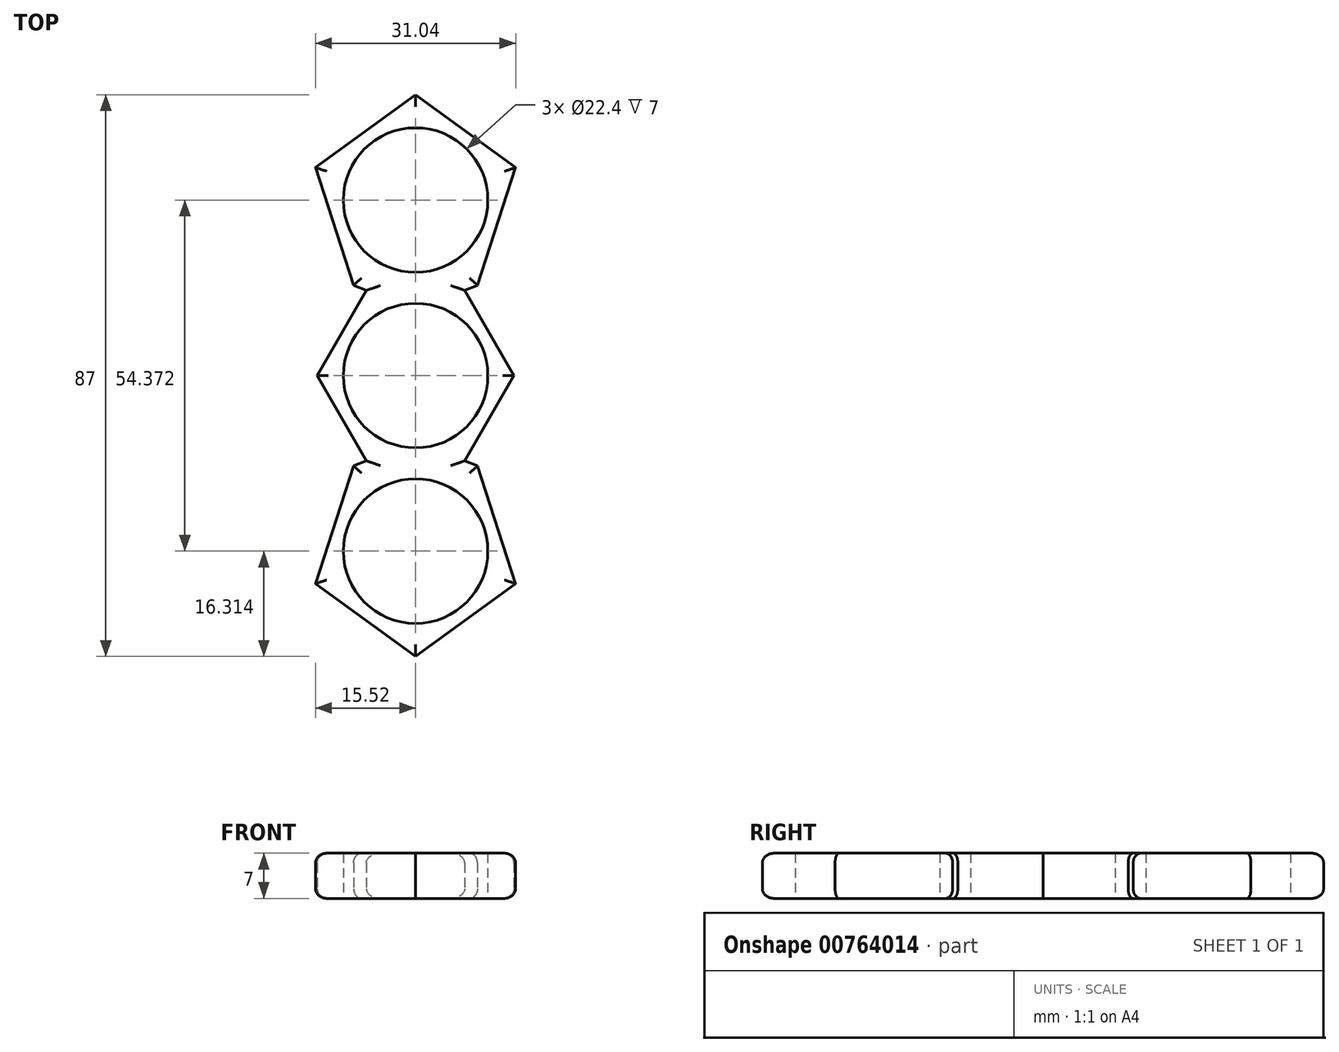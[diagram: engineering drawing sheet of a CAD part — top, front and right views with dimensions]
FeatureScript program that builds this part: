
annotation { "Feature Type Name" : "Feature", "Feature Type Description" : "" }
export const myFeature = defineFeature(function(context is Context, id is Id, definition is map)
    precondition{}
    {
        {
            var Q0;
            Q0=qCreatedBy(makeId("Top.planeOp"),FACE);
            var sketch = newSketch(context, id + "F0", { "sketchPlane" : qUnion([Q0])});
            skCircle(sketch, "E0", {"center": v(0, 0) * mm, "radius": 11.2 * mm});
            skCircle(sketch, "E1", {"center": v(0, 27.19) * mm, "radius": 11.2 * mm});
            skCircle(sketch, "E2.1.1", {"center": v(0, -27.19) * mm, "radius": 11.2 * mm});
            skLineSegment(sketch, "E3.1", {"start": v(-9.6, 13.99) * mm, "end": v(-15.52, 32.23) * mm});
            skLineSegment(sketch, "E3.2", {"start": v(-15.52, 32.23) * mm, "end": v(0, 43.5) * mm});
            skLineSegment(sketch, "E3.3", {"start": v(0, 43.5) * mm, "end": v(15.52, 32.23) * mm});
            skLineSegment(sketch, "E3.4", {"start": v(15.52, 32.23) * mm, "end": v(9.6, 13.99) * mm});
            skPoint(sketch, "E3.0.midPoint", {"position": v(0, 13.99) * mm});
            skLineSegment(sketch, "E4.1.1", {"start": v(-15.52, -32.23) * mm, "end": v(-9.6, -13.99) * mm});
            skLineSegment(sketch, "E4.1.2", {"start": v(0, -43.5) * mm, "end": v(-15.52, -32.23) * mm});
            skLineSegment(sketch, "E4.1.3", {"start": v(15.52, -32.23) * mm, "end": v(0, -43.5) * mm});
            skLineSegment(sketch, "E4.1.4", {"start": v(9.6, -13.99) * mm, "end": v(15.52, -32.23) * mm});
            skLineSegment(sketch, "E5.0", {"start": v(15.24, 0) * mm, "end": v(7.62, -13.2) * mm});
            skLineSegment(sketch, "E5.2", {"start": v(-7.62, -13.2) * mm, "end": v(-15.24, 0) * mm});
            skLineSegment(sketch, "E5.3", {"start": v(-15.24, 0) * mm, "end": v(-7.62, 13.2) * mm});
            skLineSegment(sketch, "E5.5", {"start": v(7.62, 13.2) * mm, "end": v(15.24, 0) * mm});
            skPoint(sketch, "E5.0.midPoint", {"position": v(11.43, -6.6) * mm});
            skLineSegment(sketch, "E6", {"start": v(-9.6, -13.99) * mm, "end": v(-7.62, -13.2) * mm});
            skLineSegment(sketch, "E7", {"start": v(9.6, -13.99) * mm, "end": v(7.62, -13.2) * mm});
            skLineSegment(sketch, "E8", {"start": v(7.62, 13.2) * mm, "end": v(9.6, 13.99) * mm});
            skLineSegment(sketch, "E9", {"start": v(-7.62, 13.2) * mm, "end": v(-9.6, 13.99) * mm});
            skSolve(sketch);
        }
        {
            var Q0;
            Q0=makeQuery(id+"F0.imprint","IMPRINT",FACE,{"disambiguationData":[TD([[makeQuery(id+"F0.imprint","IMPRINT",EDGE,{"derivedFrom":sQuery(id+"F0.wireOp",EDGE,"E0")}),-1.0]])]});
            extrude(context, id + "F1", {"entities" : qUnion([Q0]), "depth" : 7 * mm, "offsetDistance" : 25 * mm});
        }
        {
            var Q0;
            Q0=makeQuery(id+"F1.opExtrude","CAP_EDGE",EDGE,{"disambiguationData":[OSD([sQuery(id+"F0.wireOp",EDGE,"E4.1.1")])],"isStart":false});
            var Q1;
            Q1=makeQuery(id+"F1.opExtrude","CAP_EDGE",EDGE,{"disambiguationData":[OSD([sQuery(id+"F0.wireOp",EDGE,"E4.1.2")])],"isStart":false});
            var Q2;
            Q2=makeQuery(id+"F1.opExtrude","CAP_EDGE",EDGE,{"disambiguationData":[OSD([sQuery(id+"F0.wireOp",EDGE,"E4.1.3")])],"isStart":false});
            var Q3;
            Q3=makeQuery(id+"F1.opExtrude","CAP_EDGE",EDGE,{"disambiguationData":[OSD([sQuery(id+"F0.wireOp",EDGE,"E4.1.4")])],"isStart":false});
            var Q4;
            Q4=makeQuery(id+"F1.opExtrude","CAP_EDGE",EDGE,{"disambiguationData":[OSD([sQuery(id+"F0.wireOp",EDGE,"E6")])],"isStart":false});
            var Q5;
            Q5=makeQuery(id+"F1.opExtrude","CAP_EDGE",EDGE,{"disambiguationData":[OSD([sQuery(id+"F0.wireOp",EDGE,"E7")])],"isStart":false});
            var Q6;
            Q6=makeQuery(id+"F1.opExtrude","CAP_EDGE",EDGE,{"disambiguationData":[OSD([sQuery(id+"F0.wireOp",EDGE,"E8")])],"isStart":false});
            var Q7;
            Q7=makeQuery(id+"F1.opExtrude","CAP_EDGE",EDGE,{"disambiguationData":[OSD([sQuery(id+"F0.wireOp",EDGE,"E9")])],"isStart":false});
            var Q8;
            Q8=makeQuery(id+"F1.opExtrude","CAP_EDGE",EDGE,{"disambiguationData":[OSD([sQuery(id+"F0.wireOp",EDGE,"E5.3")])],"isStart":false});
            var Q9;
            Q9=makeQuery(id+"F1.opExtrude","CAP_EDGE",EDGE,{"disambiguationData":[OSD([sQuery(id+"F0.wireOp",EDGE,"E5.2")])],"isStart":false});
            var Q10;
            Q10=makeQuery(id+"F1.opExtrude","CAP_EDGE",EDGE,{"disambiguationData":[OSD([sQuery(id+"F0.wireOp",EDGE,"E5.0")])],"isStart":false});
            var Q11;
            Q11=makeQuery(id+"F1.opExtrude","CAP_EDGE",EDGE,{"disambiguationData":[OSD([sQuery(id+"F0.wireOp",EDGE,"E5.5")])],"isStart":false});
            var Q12;
            Q12=makeQuery(id+"F1.opExtrude","CAP_EDGE",EDGE,{"disambiguationData":[OSD([sQuery(id+"F0.wireOp",EDGE,"E3.4")])],"isStart":false});
            var Q13;
            Q13=makeQuery(id+"F1.opExtrude","CAP_EDGE",EDGE,{"disambiguationData":[OSD([sQuery(id+"F0.wireOp",EDGE,"E3.3")])],"isStart":false});
            var Q14;
            Q14=makeQuery(id+"F1.opExtrude","CAP_EDGE",EDGE,{"disambiguationData":[OSD([sQuery(id+"F0.wireOp",EDGE,"E3.2")])],"isStart":false});
            var Q15;
            Q15=makeQuery(id+"F1.opExtrude","CAP_EDGE",EDGE,{"disambiguationData":[OSD([sQuery(id+"F0.wireOp",EDGE,"E3.1")])],"isStart":false});
            fillet(context, id + "F2", {"entities" : qUnion([Q0, Q1, Q2, Q3, Q4, Q5, Q6, Q7, Q8, Q9, Q10, Q11, Q12, Q13, Q14, Q15]), "radius" : 1.5 * mm, "tangentPropagation" : true, "allowEdgeOverflow" : false});
        }
        {
            var Q0;
            Q0=makeQuery(id+"F1.opExtrude","CAP_EDGE",EDGE,{"disambiguationData":[OSD([sQuery(id+"F0.wireOp",EDGE,"E4.1.2")])],"isStart":true});
            var Q1;
            Q1=makeQuery(id+"F1.opExtrude","CAP_EDGE",EDGE,{"disambiguationData":[OSD([sQuery(id+"F0.wireOp",EDGE,"E4.1.1")])],"isStart":true});
            var Q2;
            Q2=makeQuery(id+"F1.opExtrude","CAP_EDGE",EDGE,{"disambiguationData":[OSD([sQuery(id+"F0.wireOp",EDGE,"E4.1.4")])],"isStart":true});
            var Q3;
            Q3=makeQuery(id+"F1.opExtrude","CAP_EDGE",EDGE,{"disambiguationData":[OSD([sQuery(id+"F0.wireOp",EDGE,"E4.1.3")])],"isStart":true});
            var Q4;
            Q4=makeQuery(id+"F1.opExtrude","CAP_EDGE",EDGE,{"disambiguationData":[OSD([sQuery(id+"F0.wireOp",EDGE,"E6")])],"isStart":true});
            var Q5;
            Q5=makeQuery(id+"F1.opExtrude","CAP_EDGE",EDGE,{"disambiguationData":[OSD([sQuery(id+"F0.wireOp",EDGE,"E9")])],"isStart":true});
            var Q6;
            Q6=makeQuery(id+"F1.opExtrude","CAP_EDGE",EDGE,{"disambiguationData":[OSD([sQuery(id+"F0.wireOp",EDGE,"E8")])],"isStart":true});
            var Q7;
            Q7=makeQuery(id+"F1.opExtrude","CAP_EDGE",EDGE,{"disambiguationData":[OSD([sQuery(id+"F0.wireOp",EDGE,"E7")])],"isStart":true});
            var Q8;
            Q8=makeQuery(id+"F1.opExtrude","CAP_EDGE",EDGE,{"disambiguationData":[OSD([sQuery(id+"F0.wireOp",EDGE,"E5.0")])],"isStart":true});
            var Q9;
            Q9=makeQuery(id+"F1.opExtrude","CAP_EDGE",EDGE,{"disambiguationData":[OSD([sQuery(id+"F0.wireOp",EDGE,"E3.1")])],"isStart":true});
            var Q10;
            Q10=makeQuery(id+"F1.opExtrude","CAP_EDGE",EDGE,{"disambiguationData":[OSD([sQuery(id+"F0.wireOp",EDGE,"E3.2")])],"isStart":true});
            var Q11;
            Q11=makeQuery(id+"F1.opExtrude","CAP_EDGE",EDGE,{"disambiguationData":[OSD([sQuery(id+"F0.wireOp",EDGE,"E3.3")])],"isStart":true});
            var Q12;
            Q12=makeQuery(id+"F1.opExtrude","CAP_EDGE",EDGE,{"disambiguationData":[OSD([sQuery(id+"F0.wireOp",EDGE,"E3.4")])],"isStart":true});
            var Q13;
            Q13=makeQuery(id+"F1.opExtrude","CAP_EDGE",EDGE,{"disambiguationData":[OSD([sQuery(id+"F0.wireOp",EDGE,"E5.3")])],"isStart":true});
            var Q14;
            Q14=makeQuery(id+"F1.opExtrude","CAP_EDGE",EDGE,{"disambiguationData":[OSD([sQuery(id+"F0.wireOp",EDGE,"E5.2")])],"isStart":true});
            var Q15;
            Q15=makeQuery(id+"F1.opExtrude","CAP_EDGE",EDGE,{"disambiguationData":[OSD([sQuery(id+"F0.wireOp",EDGE,"E5.5")])],"isStart":true});
            fillet(context, id + "F3", {"entities" : qUnion([Q0, Q1, Q2, Q3, Q4, Q5, Q6, Q7, Q8, Q9, Q10, Q11, Q12, Q13, Q14, Q15]), "radius" : 1.5 * mm, "tangentPropagation" : true, "allowEdgeOverflow" : false});
        }
    });
